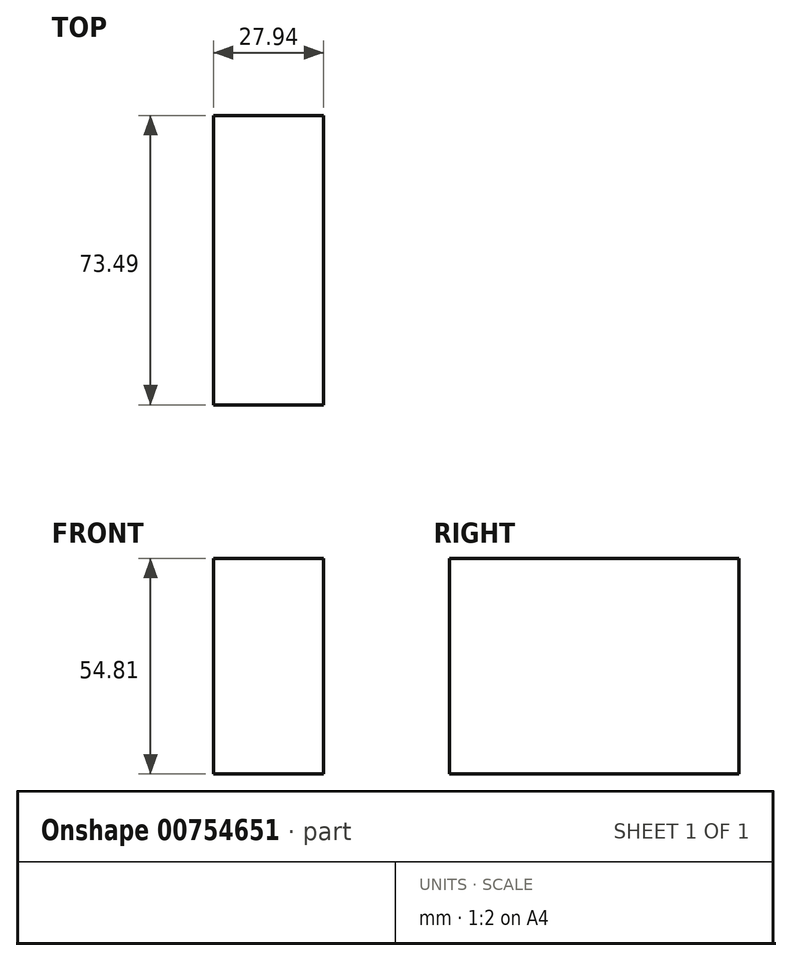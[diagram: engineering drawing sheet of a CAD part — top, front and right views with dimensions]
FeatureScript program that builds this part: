
annotation { "Feature Type Name" : "Feature", "Feature Type Description" : "" }
export const myFeature = defineFeature(function(context is Context, id is Id, definition is map)
    precondition{}
    {
        {
            var Q0;
            Q0=qCreatedBy(makeId("Right.planeOp"),FACE);
            var sketch = newSketch(context, id + "F0", { "sketchPlane" : qUnion([Q0])});
            skLineSegment(sketch, "E0.bottom", {"start": v(-43.44, 36.04) * mm, "end": v(30.05, 36.04) * mm});
            skLineSegment(sketch, "E0.top", {"start": v(-43.44, -18.77) * mm, "end": v(30.05, -18.77) * mm});
            skLineSegment(sketch, "E0.left", {"start": v(-43.44, 36.04) * mm, "end": v(-43.44, -18.77) * mm});
            skLineSegment(sketch, "E0.right", {"start": v(30.05, 36.04) * mm, "end": v(30.05, -18.77) * mm});
            skSolve(sketch);
        }
        {
            var Q0;
            Q0 = qSketchRegion(id + "F0", true);
            extrude(context, id + "F1", {"entities" : qUnion([Q0]), "depth" : 27.94 * mm, "offsetDistance" : 25.4 * mm});
        }
    });
